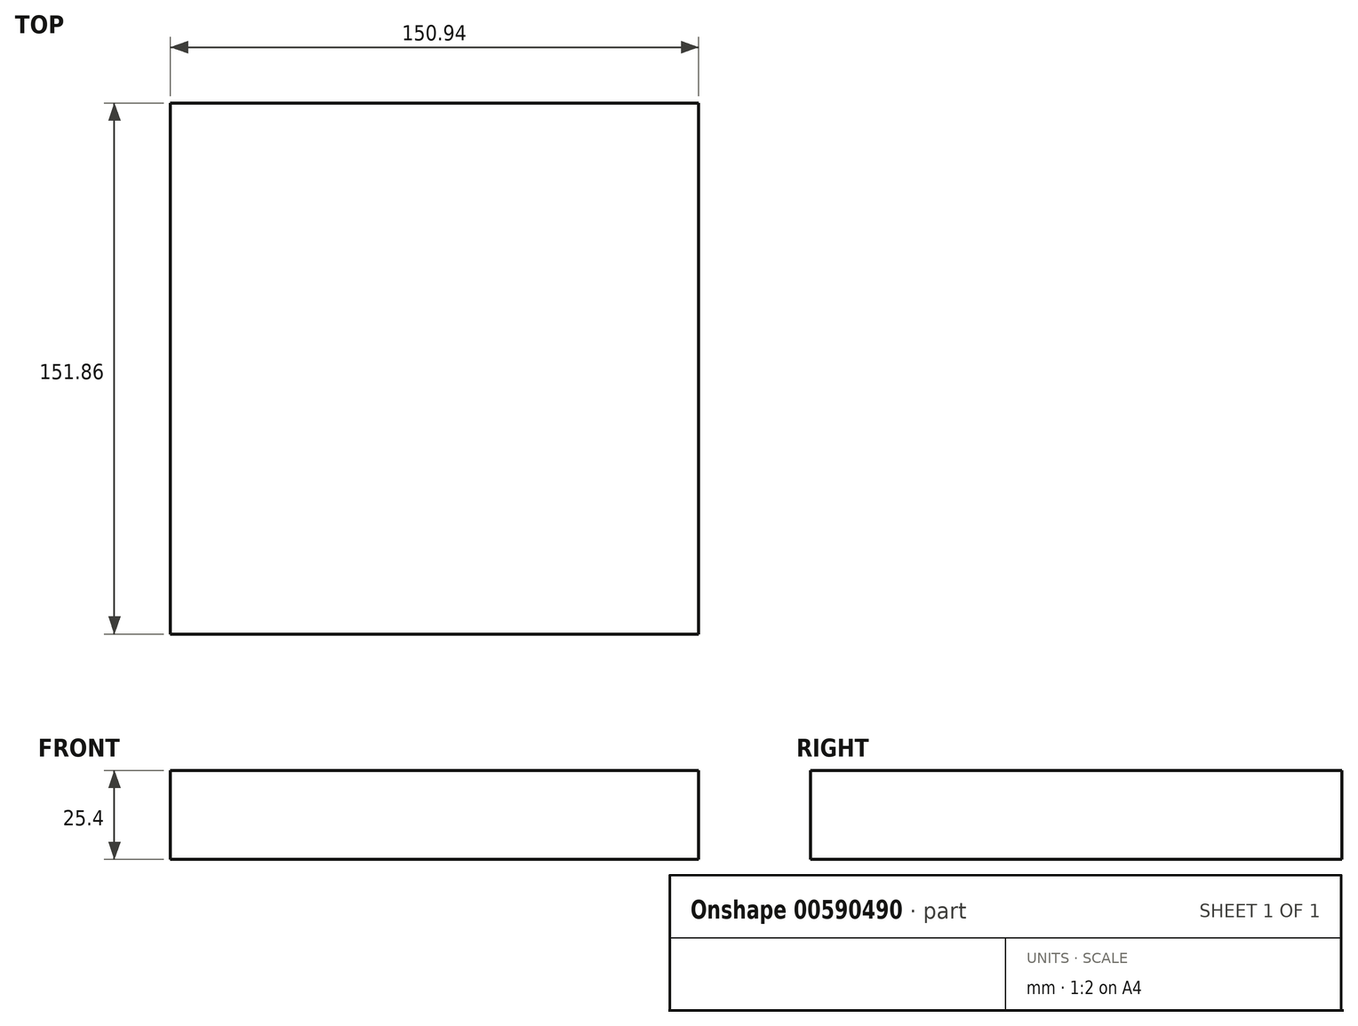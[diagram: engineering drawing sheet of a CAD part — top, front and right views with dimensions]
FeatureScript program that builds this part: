
annotation { "Feature Type Name" : "Feature", "Feature Type Description" : "" }
export const myFeature = defineFeature(function(context is Context, id is Id, definition is map)
    precondition{}
    {
        {
            var Q0;
            Q0=qCreatedBy(makeId("Top.planeOp"),FACE);
            var sketch = newSketch(context, id + "F0", { "sketchPlane" : qUnion([Q0])});
            skLineSegment(sketch, "E0.bottom", {"start": v(-75.56, 76.31) * mm, "end": v(75.38, 76.31) * mm});
            skLineSegment(sketch, "E0.top", {"start": v(-75.56, -75.55) * mm, "end": v(75.38, -75.55) * mm});
            skLineSegment(sketch, "E0.left", {"start": v(-75.56, 76.31) * mm, "end": v(-75.56, -75.55) * mm});
            skLineSegment(sketch, "E0.right", {"start": v(75.38, 76.31) * mm, "end": v(75.38, -75.55) * mm});
            skSolve(sketch);
        }
        {
            var Q0;
            Q0 = qSketchRegion(id + "F0", true);
            extrude(context, id + "F1", {"entities" : qUnion([Q0]), "depth" : 25.4 * mm, "offsetDistance" : 25.4 * mm});
        }
    });
